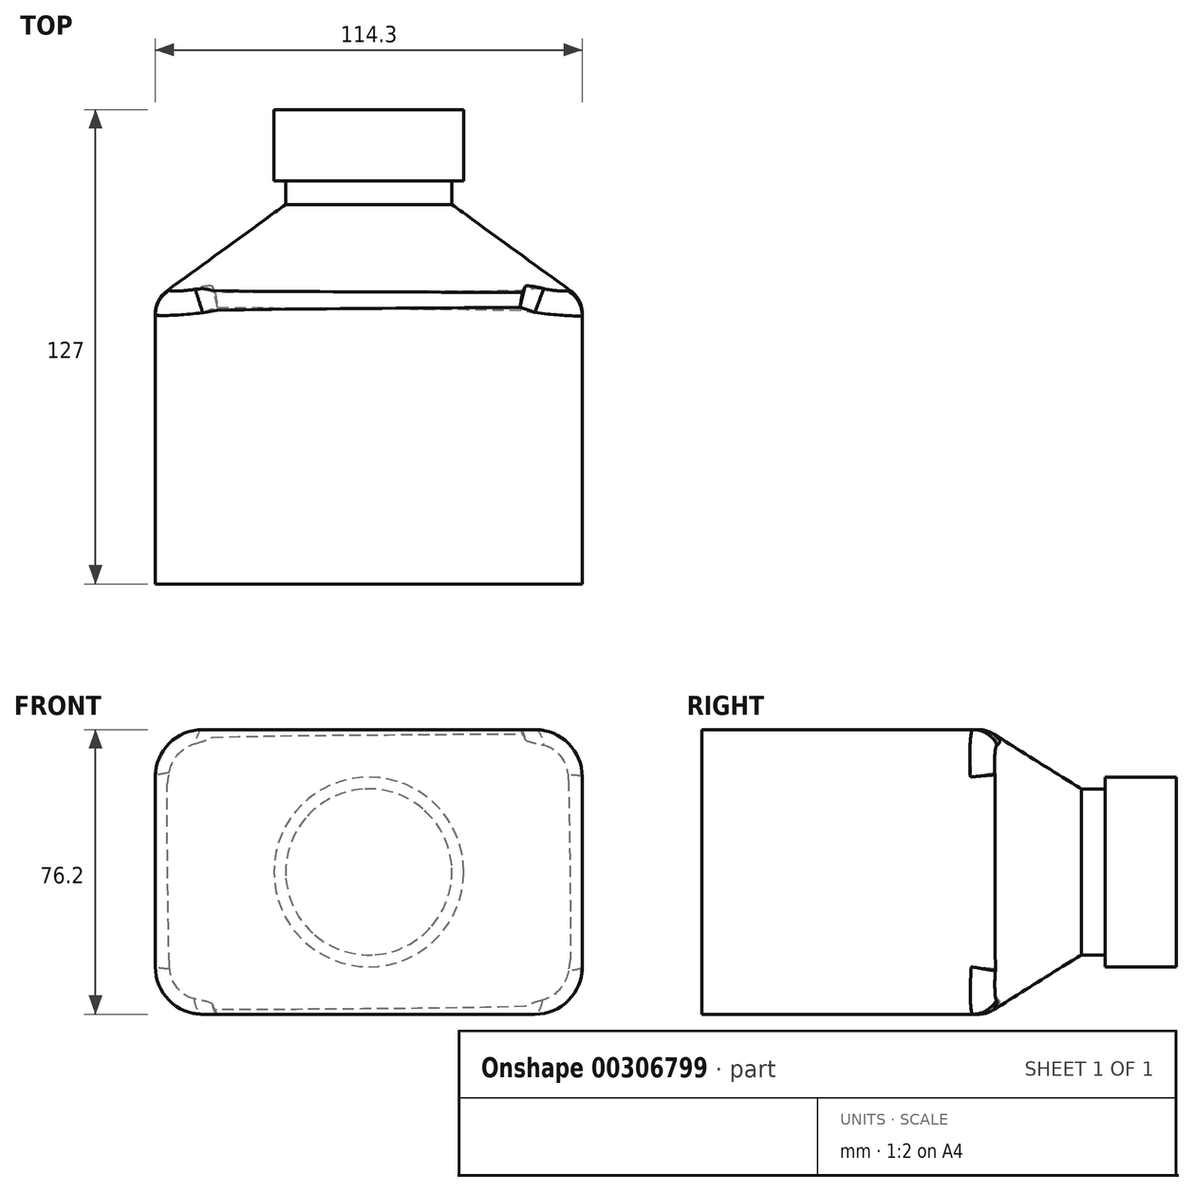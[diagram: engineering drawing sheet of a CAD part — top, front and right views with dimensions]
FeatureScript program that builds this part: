
annotation { "Feature Type Name" : "Feature", "Feature Type Description" : "" }
export const myFeature = defineFeature(function(context is Context, id is Id, definition is map)
    precondition{}
    {
        {
            var Q0;
            Q0=qCreatedBy(makeId("Top.planeOp"),FACE);
            var sketch = newSketch(context, id + "F0", { "sketchPlane" : qUnion([Q0])});
            skLineSegment(sketch, "E0.bottom", {"start": v(44.45, 38.1) * mm, "end": v(-44.45, 38.1) * mm});
            skLineSegment(sketch, "E0.top", {"start": v(44.45, -38.1) * mm, "end": v(-44.45, -38.1) * mm});
            skLineSegment(sketch, "E0.left", {"start": v(57.15, 25.4) * mm, "end": v(57.15, -25.4) * mm});
            skLineSegment(sketch, "E0.right", {"start": v(-57.15, 25.4) * mm, "end": v(-57.15, -25.4) * mm});
            skPoint(sketch, "E0.middle", {"position": v(0, 0) * mm});
            skPoint(sketch, "E1.visualSharp", {"position": v(-57.15, 38.1) * mm});
            skArc(sketch, "E1.filletArc", {"start": v(-44.45, 38.1) * mm, "mid": v(-53.43, 34.38) * mm, "end": v(-57.15, 25.4) * mm});
            skPoint(sketch, "E2.visualSharp", {"position": v(-57.15, -38.1) * mm});
            skArc(sketch, "E2.filletArc", {"start": v(-57.15, -25.4) * mm, "mid": v(-53.43, -34.38) * mm, "end": v(-44.45, -38.1) * mm});
            skPoint(sketch, "E3.visualSharp", {"position": v(57.15, -38.1) * mm});
            skArc(sketch, "E3.filletArc", {"start": v(44.45, -38.1) * mm, "mid": v(53.43, -34.38) * mm, "end": v(57.15, -25.4) * mm});
            skPoint(sketch, "E4.visualSharp", {"position": v(57.15, 38.1) * mm});
            skArc(sketch, "E4.filletArc", {"start": v(57.15, 25.4) * mm, "mid": v(53.43, 34.38) * mm, "end": v(44.45, 38.1) * mm});
            skSolve(sketch);
        }
        {
            var Q0;
            Q0=qCreatedBy(makeId("Top.planeOp"),FACE);
            cPlane(context, id + "F1", {"entities" : qUnion([Q0]), "cplaneType" : CPlaneType.OFFSET, "offset" : 76.2 * mm, "width" : 152.4 * mm, "height" : 152.4 * mm});
        }
        {
            var Q0;
            Q0=qCreatedBy(id+"F1.planeOp",FACE);
            var sketch = newSketch(context, id + "F2", { "sketchPlane" : qUnion([Q0])});
            skLineSegment(sketch, "E5.bottom", {"start": v(44.45, 38.1) * mm, "end": v(-44.45, 38.1) * mm});
            skLineSegment(sketch, "E5.top", {"start": v(44.45, -38.1) * mm, "end": v(-44.45, -38.1) * mm});
            skLineSegment(sketch, "E5.left", {"start": v(57.15, 25.4) * mm, "end": v(57.15, -25.4) * mm});
            skLineSegment(sketch, "E5.right", {"start": v(-57.15, 25.4) * mm, "end": v(-57.15, -25.4) * mm});
            skPoint(sketch, "E5.middle", {"position": v(0, 0) * mm});
            skPoint(sketch, "E6.visualSharp", {"position": v(-57.15, 38.1) * mm});
            skArc(sketch, "E6.filletArc", {"start": v(-44.45, 38.1) * mm, "mid": v(-53.43, 34.38) * mm, "end": v(-57.15, 25.4) * mm});
            skPoint(sketch, "E7.visualSharp", {"position": v(-57.15, -38.1) * mm});
            skArc(sketch, "E7.filletArc", {"start": v(-57.15, -25.4) * mm, "mid": v(-53.43, -34.38) * mm, "end": v(-44.45, -38.1) * mm});
            skPoint(sketch, "E8.visualSharp", {"position": v(57.15, -38.1) * mm});
            skArc(sketch, "E8.filletArc", {"start": v(44.45, -38.1) * mm, "mid": v(53.43, -34.38) * mm, "end": v(57.15, -25.4) * mm});
            skPoint(sketch, "E9.visualSharp", {"position": v(57.15, 38.1) * mm});
            skArc(sketch, "E9.filletArc", {"start": v(57.15, 25.4) * mm, "mid": v(53.43, 34.38) * mm, "end": v(44.45, 38.1) * mm});
            skSolve(sketch);
        }
        {
            var Q0;
            Q0=qCreatedBy(id+"F1.planeOp",FACE);
            cPlane(context, id + "F3", {"entities" : qUnion([Q0]), "cplaneType" : CPlaneType.OFFSET, "offset" : 25.4 * mm, "width" : 152.4 * mm, "height" : 152.4 * mm});
        }
        {
            var Q0;
            Q0=qCreatedBy(id+"F3.planeOp",FACE);
            var sketch = newSketch(context, id + "F4", { "sketchPlane" : qUnion([Q0])});
            skCircle(sketch, "E10", {"center": v(0, 0) * mm, "radius": 22.23 * mm});
            skSolve(sketch);
        }
        {
            var Q0;
            Q0=makeQuery(id+"F0.imprint","IMPRINT",FACE,{"disambiguationData":[TD([[makeQuery(id+"F0.imprint","IMPRINT",EDGE,{"derivedFrom":sQuery(id+"F0.wireOp",EDGE,"E0.bottom")}),1.0]])]});
            var Q1;
            Q1=makeQuery(id+"F2.imprint","IMPRINT",FACE,{"disambiguationData":[TD([[makeQuery(id+"F2.imprint","IMPRINT",EDGE,{"derivedFrom":sQuery(id+"F2.wireOp",EDGE,"E5.bottom")}),1.0]])]});
            loft(context, id + "F5", {"sheetProfilesArray" : [{ "sheetProfileEntities" : qUnion([Q0]) }, { "sheetProfileEntities" : qUnion([Q1]) }]});
        }
        {
            var Q1;
            Q1=makeQuery(id+"F5.opLoft","CAP_FACE",FACE,{"disambiguationData":[OSD([makeQuery(id+"F2.imprint","IMPRINT",FACE,{"disambiguationData":[TD([[makeQuery(id+"F2.imprint","IMPRINT",EDGE,{"derivedFrom":sQuery(id+"F2.wireOp",EDGE,"E5.bottom")}),1.0]])]})])],"isStart":true});
            var Q2;
            Q2=makeQuery(id+"F4.imprint","IMPRINT",FACE,{"disambiguationData":[TD([[makeQuery(id+"F4.imprint","IMPRINT",EDGE,{"derivedFrom":sQuery(id+"F4.wireOp",EDGE,"E10")}),1.0]])]});
            loft(context, id + "F6", {"operationType" : NewBodyOperationType.ADD, "sheetProfilesArray" : [{ "sheetProfileEntities" : qUnion([Q1]) }, { "sheetProfileEntities" : qUnion([Q2]) }]});
        }
        {
            var Q0;
            Q0=qCreatedBy(id+"F3.planeOp",FACE);
            cPlane(context, id + "F7", {"entities" : qUnion([Q0]), "cplaneType" : CPlaneType.OFFSET, "offset" : 6.35 * mm, "width" : 152.4 * mm, "height" : 152.4 * mm});
        }
        {
            var Q0;
            Q0=qCreatedBy(id+"F7.planeOp",FACE);
            var sketch = newSketch(context, id + "F8", { "sketchPlane" : qUnion([Q0])});
            skCircle(sketch, "E11", {"center": v(0, 0) * mm, "radius": 22.23 * mm});
            skSolve(sketch);
        }
        {
            var Q1;
            Q1=makeQuery(id+"F6.opLoft","CAP_FACE",FACE,{"disambiguationData":[OSD([makeQuery(id+"F4.imprint","IMPRINT",FACE,{"disambiguationData":[TD([[makeQuery(id+"F4.imprint","IMPRINT",EDGE,{"derivedFrom":sQuery(id+"F4.wireOp",EDGE,"E10")}),1.0]])]})])],"isStart":true});
            var Q2;
            Q2=makeQuery(id+"F8.imprint","IMPRINT",FACE,{"disambiguationData":[TD([[makeQuery(id+"F8.imprint","IMPRINT",EDGE,{"derivedFrom":sQuery(id+"F8.wireOp",EDGE,"E11")}),1.0]])]});
            loft(context, id + "F9", {"operationType" : NewBodyOperationType.ADD, "sheetProfilesArray" : [{ "sheetProfileEntities" : qUnion([Q1]) }, { "sheetProfileEntities" : qUnion([Q2]) }]});
        }
        {
            var Q0;
            Q0=qCreatedBy(id+"F7.planeOp",FACE);
            var sketch = newSketch(context, id + "F10", { "sketchPlane" : qUnion([Q0])});
            skCircle(sketch, "E12", {"center": v(0, 0) * mm, "radius": 25.4 * mm});
            skSolve(sketch);
        }
        {
            var Q0;
            Q0=makeQuery(id+"F10.imprint","IMPRINT",FACE,{"disambiguationData":[TD([[makeQuery(id+"F10.imprint","IMPRINT",EDGE,{"derivedFrom":sQuery(id+"F10.wireOp",EDGE,"E12")}),1.0]])]});
            extrude(context, id + "F11", {"entities" : qUnion([Q0]), "operationType" : NewBodyOperationType.ADD, "depth" : 19.05 * mm});
        }
        {
            var Q0;
            {var subQ0=sQuery(id+"F2.wireOp",EDGE,"E8.filletArc");var subQ1=sQuery(id+"F2.wireOp",EDGE,"E7.filletArc");var subQ2=sQuery(id+"F2.wireOp",EDGE,"E5.top");Q0=makeQuery(id+"F6.boolean.opBoolean","MERGE",EDGE,{"derivedFrom":[makeQuery(id+"F5.opLoft","MID_CAP_EDGE",EDGE,{"disambiguationData":[OSD([subQ2,subQ1,subQ0])],"capPos":1.0}),makeQuery(id+"F6.opLoft","MID_CAP_EDGE",EDGE,{"disambiguationData":[OSD([subQ2,subQ1,subQ0])],"capPos":0.0})]});}
            var Q1;
            {var subQ0=sQuery(id+"F2.wireOp",EDGE,"E7.filletArc");var subQ1=sQuery(id+"F2.wireOp",EDGE,"E5.right");var subQ2=sQuery(id+"F2.wireOp",EDGE,"E5.top");Q1=makeQuery(id+"F6.boolean.opBoolean","MERGE",EDGE,{"derivedFrom":[makeQuery(id+"F5.opLoft","MID_CAP_EDGE",EDGE,{"disambiguationData":[OSD([subQ2,subQ1,subQ0])],"capPos":1.0}),makeQuery(id+"F6.opLoft","MID_CAP_EDGE",EDGE,{"disambiguationData":[OSD([subQ2,subQ1,subQ0])],"capPos":0.0})]});}
            fillet(context, id + "F12", {"entities" : qUnion([Q0, Q1]), "radius" : 7.62 * mm, "tangentPropagation" : true, "allowEdgeOverflow" : false});
        }
        {
            var Q0;
            Q0=qCreatedBy(makeId("Top.planeOp"),FACE);
            cPlane(context, id + "F13", {"entities" : qUnion([Q0]), "cplaneType" : CPlaneType.OFFSET, "offset" : 6.35 * mm, "width" : 152.4 * mm, "height" : 152.4 * mm});
        }
        {
            var Q0;
            Q0=makeQuery(id+"F5.opLoft","SWEPT_BODY",BODY,{"disambiguationData":[OSD([makeQuery(id+"F0.imprint","IMPRINT",FACE,{"disambiguationData":[TD([[makeQuery(id+"F0.imprint","IMPRINT",EDGE,{"derivedFrom":sQuery(id+"F0.wireOp",EDGE,"E0.bottom")}),1.0]])]}),makeQuery(id+"F2.imprint","IMPRINT",FACE,{"disambiguationData":[TD([[makeQuery(id+"F2.imprint","IMPRINT",EDGE,{"derivedFrom":sQuery(id+"F2.wireOp",EDGE,"E5.bottom")}),1.0]])]})])]});
            var Q1;
            Q1=makeQuery(id+"F5.opLoft","MID_CAP_EDGE",EDGE,{"disambiguationData":[OSD([sQuery(id+"F0.wireOp",EDGE,"E0.top"),sQuery(id+"F0.wireOp",EDGE,"E2.filletArc"),sQuery(id+"F0.wireOp",EDGE,"E3.filletArc")])],"capPos":0.0});
            transform(context, id + "F14", {"entities" : qUnion([Q0]), "transformType" : TransformType.ROTATION, "transformAxis" : qUnion([Q1]), "angle" : 90 * degree, "makeCopy" : false});
        }
    });
